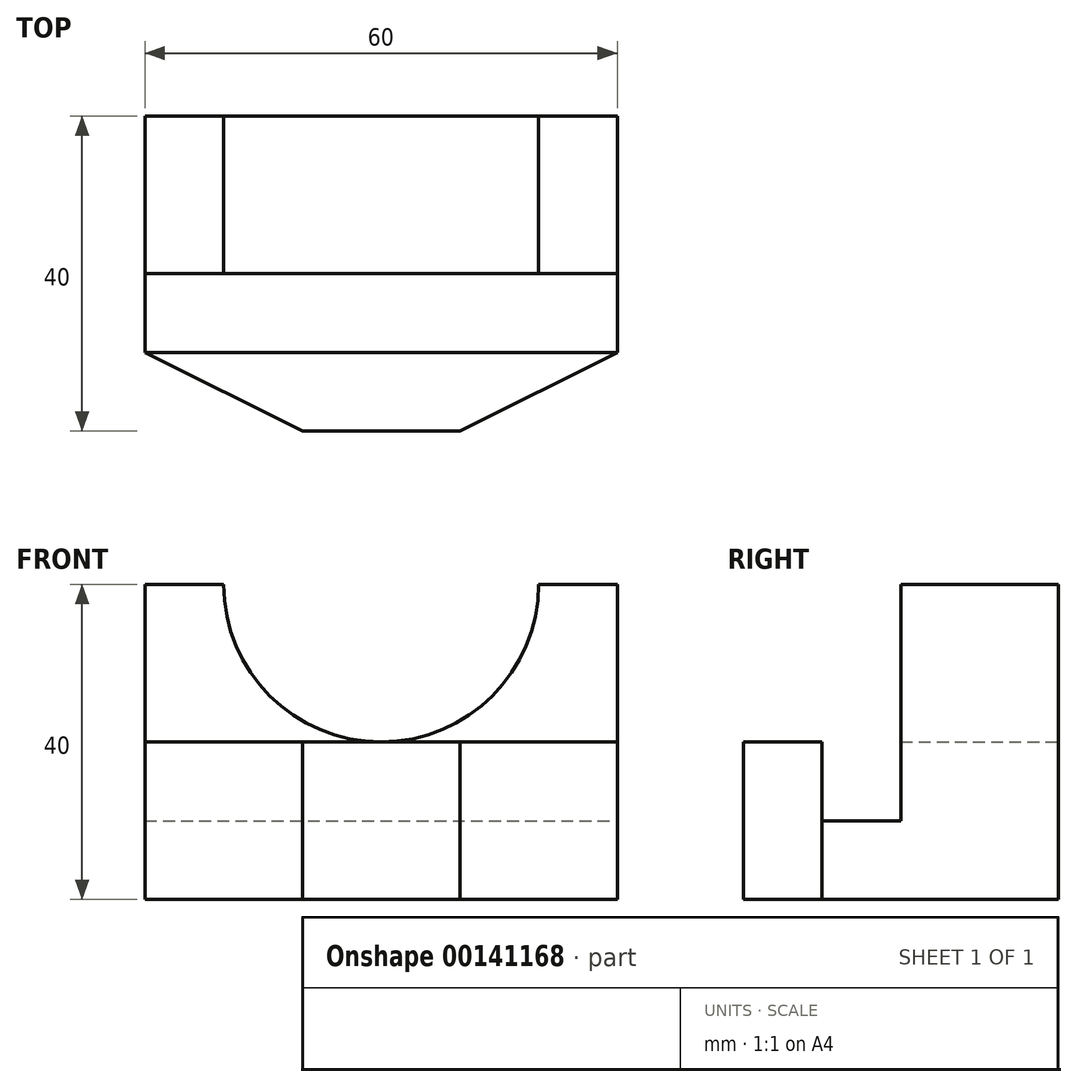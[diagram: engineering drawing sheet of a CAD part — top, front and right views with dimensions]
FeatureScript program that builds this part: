
annotation { "Feature Type Name" : "Feature", "Feature Type Description" : "" }
export const myFeature = defineFeature(function(context is Context, id is Id, definition is map)
    precondition{}
    {
        {
            var Q0;
            Q0=qCreatedBy(makeId("Top.planeOp"),FACE);
            var sketch = newSketch(context, id + "F0", { "sketchPlane" : qUnion([Q0])});
            skLineSegment(sketch, "E0.bottom", {"start": v(0, 0) * mm, "end": v(10, 0) * mm});
            skLineSegment(sketch, "E0.top", {"start": v(0, -20) * mm, "end": v(10, -20) * mm});
            skLineSegment(sketch, "E0.left", {"start": v(0, 0) * mm, "end": v(0, -20) * mm});
            skLineSegment(sketch, "E0.right", {"start": v(10, 0) * mm, "end": v(10, -20) * mm});
            skLineSegment(sketch, "E1.bottom", {"start": v(10, 0) * mm, "end": v(50, 0) * mm});
            skLineSegment(sketch, "E1.top", {"start": v(10, -20) * mm, "end": v(50, -20) * mm});
            skLineSegment(sketch, "E1.right", {"start": v(50, 0) * mm, "end": v(50, -20) * mm});
            skLineSegment(sketch, "E2.bottom", {"start": v(50, 0) * mm, "end": v(60, 0) * mm});
            skLineSegment(sketch, "E2.top", {"start": v(50, -20) * mm, "end": v(60, -20) * mm});
            skLineSegment(sketch, "E2.right", {"start": v(60, 0) * mm, "end": v(60, -20) * mm});
            skLineSegment(sketch, "E3.bottom", {"start": v(0, -20) * mm, "end": v(60, -20) * mm});
            skLineSegment(sketch, "E3.top", {"start": v(0, -30) * mm, "end": v(60, -30) * mm});
            skLineSegment(sketch, "E3.left", {"start": v(0, -20) * mm, "end": v(0, -30) * mm});
            skLineSegment(sketch, "E3.right", {"start": v(60, -20) * mm, "end": v(60, -30) * mm});
            skLineSegment(sketch, "E4", {"start": v(0, -30) * mm, "end": v(20, -40) * mm});
            skLineSegment(sketch, "E5", {"start": v(20, -40) * mm, "end": v(40, -40) * mm});
            skLineSegment(sketch, "E6", {"start": v(40, -40) * mm, "end": v(60, -30) * mm});
            skSolve(sketch);
        }
        {
            var Q0;
            Q0=makeQuery(id+"F0.imprint","IMPRINT",FACE,{"disambiguationData":[TD([[makeQuery(id+"F0.imprint","IMPRINT",EDGE,{"derivedFrom":sQuery(id+"F0.wireOp",EDGE,"E3.top")}),-1.0]])]});
            extrude(context, id + "F1", {"entities" : qUnion([Q0]), "depth" : 20 * mm});
        }
        {
            var Q0;
            Q0=makeQuery(id+"F0.imprint","IMPRINT",FACE,{"disambiguationData":[TD([[makeQuery(id+"F0.imprint","IMPRINT",EDGE,{"derivedFrom":sQuery(id+"F0.wireOp",EDGE,"E1.bottom")}),-1.0]])]});
            extrude(context, id + "F2", {"entities" : qUnion([Q0]), "operationType" : NewBodyOperationType.ADD, "depth" : 40 * mm});
        }
        {
            var Q0;
            Q0=makeQuery(id+"F0.imprint","IMPRINT",FACE,{"disambiguationData":[TD([[makeQuery(id+"F0.imprint","IMPRINT",EDGE,{"derivedFrom":sQuery(id+"F0.wireOp",EDGE,"E3.top")}),1.0]])]});
            extrude(context, id + "F3", {"entities" : qUnion([Q0]), "operationType" : NewBodyOperationType.ADD, "depth" : 10 * mm});
        }
        {
            var Q0;
            Q0=makeQuery(id+"F0.imprint","IMPRINT",FACE,{"disambiguationData":[TD([[makeQuery(id+"F0.imprint","IMPRINT",EDGE,{"derivedFrom":sQuery(id+"F0.wireOp",EDGE,"E0.bottom")}),-1.0]])]});
            var Q1;
            Q1=makeQuery(id+"F0.imprint","IMPRINT",FACE,{"disambiguationData":[TD([[makeQuery(id+"F0.imprint","IMPRINT",EDGE,{"derivedFrom":sQuery(id+"F0.wireOp",EDGE,"E2.bottom")}),-1.0]])]});
            extrude(context, id + "F4", {"entities" : qUnion([Q0, Q1]), "operationType" : NewBodyOperationType.ADD, "depth" : 40 * mm});
        }
        {
            var Q0;
            Q0=qCreatedBy(makeId("Front.planeOp"),FACE);
            var sketch = newSketch(context, id + "F5", { "sketchPlane" : qUnion([Q0])});
            skLineSegment(sketch, "E7.bottom", {"start": v(0, 0) * mm, "end": v(60, 0) * mm});
            skLineSegment(sketch, "E7.top", {"start": v(0, 40) * mm, "end": v(60, 40) * mm});
            skLineSegment(sketch, "E7.left", {"start": v(0, 0) * mm, "end": v(0, 40) * mm});
            skLineSegment(sketch, "E7.right", {"start": v(60, 0) * mm, "end": v(60, 40) * mm});
            skLineSegment(sketch, "E8", {"start": v(0, 40) * mm, "end": v(10, 40) * mm});
            skLineSegment(sketch, "E9", {"start": v(60, 40) * mm, "end": v(50, 40) * mm});
            skArc(sketch, "E10", {"start": v(10, 40) * mm, "mid": v(30, 20) * mm, "end": v(50, 40) * mm});
            skLineSegment(sketch, "E11", {"start": v(10, 40) * mm, "end": v(50, 40) * mm});
            skSolve(sketch);
        }
        {
            var Q0;
            Q0=makeQuery(id+"F5.imprint","IMPRINT",FACE,{"disambiguationData":[TD([[makeQuery(id+"F5.imprint","IMPRINT",EDGE,{"derivedFrom":sQuery(id+"F5.wireOp",EDGE,"E10")}),1.0]])]});
            extrude(context, id + "F6", {"entities" : qUnion([Q0]), "operationType" : NewBodyOperationType.REMOVE, "endBound" : BoundingType.THROUGH_ALL, "depth" : 25 * mm});
        }
    });
